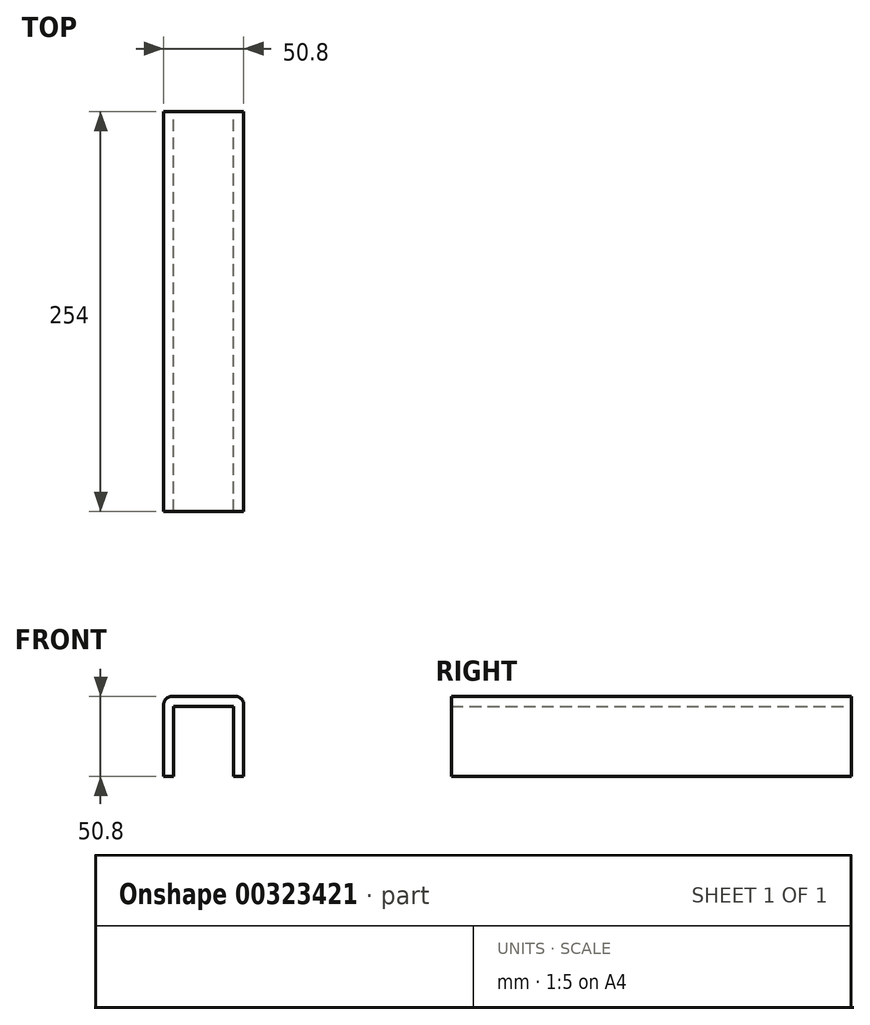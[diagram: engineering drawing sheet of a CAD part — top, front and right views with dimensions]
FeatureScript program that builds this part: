
annotation { "Feature Type Name" : "Feature", "Feature Type Description" : "" }
export const myFeature = defineFeature(function(context is Context, id is Id, definition is map)
    precondition{}
    {
        {
            var Q0;
            Q0=qCreatedBy(makeId("Front.planeOp"),FACE);
            var sketch = newSketch(context, id + "F0", { "sketchPlane" : qUnion([Q0])});
            skLineSegment(sketch, "E0", {"start": v(0, 0) * mm, "end": v(0, 50.8) * mm});
            skLineSegment(sketch, "E1", {"start": v(0, 50.8) * mm, "end": v(50.8, 50.8) * mm});
            skLineSegment(sketch, "E2", {"start": v(50.8, 50.8) * mm, "end": v(50.8, 0) * mm});
            skLineSegment(sketch, "E3.0", {"start": v(44.45, 44.45) * mm, "end": v(44.45, 0) * mm});
            skLineSegment(sketch, "E3.1", {"start": v(6.35, 44.45) * mm, "end": v(44.45, 44.45) * mm});
            skLineSegment(sketch, "E3.2", {"start": v(6.35, 0) * mm, "end": v(6.35, 44.45) * mm});
            skLineSegment(sketch, "E4", {"start": v(0, 0) * mm, "end": v(6.35, 0) * mm});
            skLineSegment(sketch, "E5", {"start": v(44.45, 0) * mm, "end": v(50.8, 0) * mm});
            skSolve(sketch);
        }
        {
            var Q0;
            Q0 = qSketchRegion(id + "F0", true);
            extrude(context, id + "F1", {"entities" : qUnion([Q0]), "endBound" : BoundingType.SYMMETRIC, "depth" : 254 * mm});
        }
        {
            var Q0;
            Q0=makeQuery(id+"F1.opExtrude","SWEPT_EDGE",EDGE,{"disambiguationData":[OSD([sQuery(id+"F0.wireOp",EDGE,"E0"),sQuery(id+"F0.wireOp",EDGE,"E1")])]});
            var Q1;
            Q1=makeQuery(id+"F1.opExtrude","SWEPT_EDGE",EDGE,{"disambiguationData":[OSD([sQuery(id+"F0.wireOp",EDGE,"E1"),sQuery(id+"F0.wireOp",EDGE,"E2")])]});
            fillet(context, id + "F2", {"entities" : qUnion([Q0, Q1]), "radius" : 5.08 * mm, "tangentPropagation" : true, "allowEdgeOverflow" : false});
        }
    });
